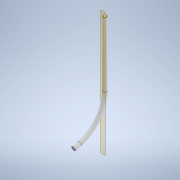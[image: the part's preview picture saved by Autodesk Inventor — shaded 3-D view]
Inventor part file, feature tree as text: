
AUTODESK INVENTOR PART (.ipt)
format: ipt  version: 2021.2 (Build 252289000, 289)  size: 137,728 bytes
history: native  units: in
note: dims shown in document units (in); Inventor stores cm internally (conversion verified against a paired STEP export)
features: sketch x5, hole x2, extrude x1, plane x1, other x1
ambient origin geometry x8: Origin, YZ Plane, XZ Plane, XY Plane, X Axis, Y Axis, Z Axis, Center Point
bodies: Solid1 (feature_tree)
feature tree (10):
  extrude  "Extrusion1"  Depth=0.25in
  sketch  "Sketch2"  dims[d2=7.0in d3=0.0in d4=1.5in]
  sketch  "Sketch3"  dims[d5=1.0in d6=1.5in d7=3.0in]
  plane  "Work Plane1"
  other  "Bend Part1"
  hole  "Hole1"  [1 undecoded]
  hole  "Hole4"  [1 undecoded]
  sketch  "Sketch1"  dims[d0=0.25in d1=0.12in]
  sketch  "Sketch4"  dims[d8=2.0in d9=75.0deg]
  sketch  "Sketch8"  dims[d10=0.156in d11=0.25in d12=0.375in d13=0.25in d14=0.5635in d15=0.25in d16=0.0in d31=0.156in d32=0.25in d33=0.507in d34=0.25in d35=0.5635in d36=0.25in d37=0.0in d17=0.75in d18=0.8108in d19=0.0625in d20=0.75in d21=0.375in]
note: 2 required parameter values undecoded (feature->parameter linkage not recoverable at this tier; creation-order binding heuristic only, values carry confidence <= 0.55)
